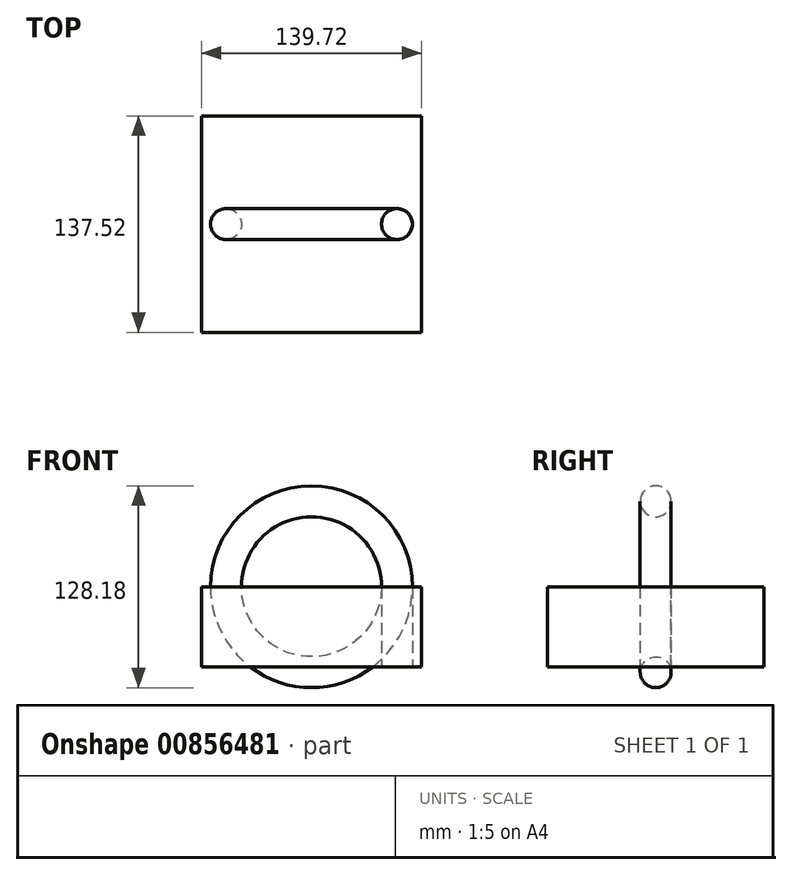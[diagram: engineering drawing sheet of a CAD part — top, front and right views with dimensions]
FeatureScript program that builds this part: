
annotation { "Feature Type Name" : "Feature", "Feature Type Description" : "" }
export const myFeature = defineFeature(function(context is Context, id is Id, definition is map)
    precondition{}
    {
        {
            var Q0;
            Q0=qCreatedBy(makeId("Top.planeOp"),FACE);
            var sketch = newSketch(context, id + "F0", { "sketchPlane" : qUnion([Q0])});
            skLineSegment(sketch, "E0.bottom", {"start": v(69.86, -68.76) * mm, "end": v(-69.86, -68.76) * mm});
            skLineSegment(sketch, "E0.top", {"start": v(69.86, 68.76) * mm, "end": v(-69.86, 68.76) * mm});
            skLineSegment(sketch, "E0.left", {"start": v(69.86, -68.76) * mm, "end": v(69.86, 68.76) * mm});
            skLineSegment(sketch, "E0.right", {"start": v(-69.86, -68.76) * mm, "end": v(-69.86, 68.76) * mm});
            skPoint(sketch, "E0.middle", {"position": v(0, 0) * mm});
            skLineSegment(sketch, "E1", {"start": v(0, 68.76) * mm, "end": v(0, -68.76) * mm});
            skSolve(sketch);
        }
        {
            var Q0;
            Q0=qCreatedBy(makeId("Top.planeOp"),FACE);
            var sketch = newSketch(context, id + "F1", { "sketchPlane" : qUnion([Q0])});
            skCircle(sketch, "E2", {"center": v(54.26, 0) * mm, "radius": 9.82 * mm});
            skSolve(sketch);
        }
        {
            var Q0;
            {var subQ0=sQuery(id+"F0.wireOp",EDGE,"E0.right");Q0=makeQuery(id+"F0.imprint","IMPRINT",FACE,{"disambiguationData":[TD([[makeQuery(id+"F0.imprint","IMPRINT",EDGE,{"derivedFrom":subQ0}),-1.0]])]});}
            var Q1;
            {var subQ0=sQuery(id+"F0.wireOp",EDGE,"E0.left");Q1=makeQuery(id+"F0.imprint","IMPRINT",FACE,{"disambiguationData":[TD([[makeQuery(id+"F0.imprint","IMPRINT",EDGE,{"derivedFrom":subQ0}),1.0]])]});}
            var Q2;
            Q2=makeQuery(id+"F1.imprint","IMPRINT",FACE,{"disambiguationData":[TD([[makeQuery(id+"F1.imprint","IMPRINT",EDGE,{"derivedFrom":sQuery(id+"F1.wireOp",EDGE,"E2")}),1.0]])]});
            extrude(context, id + "F2", {"entities" : qUnion([Q0, Q1, Q2]), "depth" : 50.8 * mm, "offsetDistance" : 25.4 * mm});
        }
        {
            var Q0;
            Q0=sQuery(id+"F0.wireOp",EDGE,"E1");
            extrude(context, id + "F3", {"bodyType" : ToolBodyType.SURFACE, "surfaceEntities" : qUnion([Q0]), "depth" : 50.8 * mm, "offsetDistance" : 25.4 * mm});
        }
        {
            var Q0;
            Q0=makeQuery(id+"F2.opExtrude","CAP_FACE",FACE,{"disambiguationData":[OSD([sQuery(id+"F1.wireOp",EDGE,"E2")])],"isStart":false});
            var Q1;
            Q1=makeQuery(id+"F3.opExtrude","CAP_EDGE",EDGE,{"disambiguationData":[OSD([sQuery(id+"F0.wireOp",EDGE,"E1")])],"isStart":false});
            revolve(context, id + "F4", {"surfaceOperationType" : NewSurfaceOperationType.NEW, "entities" : qUnion([Q0]), "axis" : qUnion([Q1]), "revolveType" : RevolveType.FULL});
        }
    });
